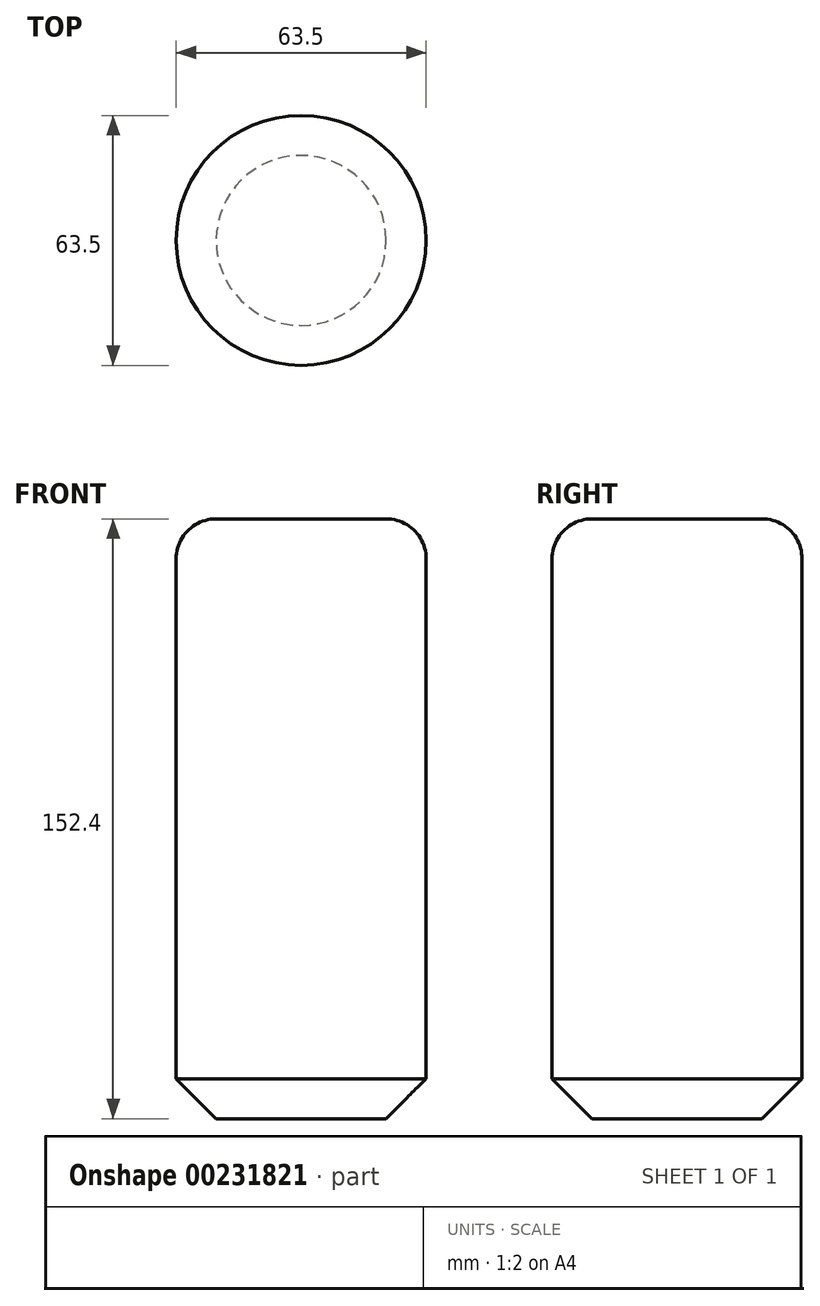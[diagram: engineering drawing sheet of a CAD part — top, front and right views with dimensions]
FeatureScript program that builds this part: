
annotation { "Feature Type Name" : "Feature", "Feature Type Description" : "" }
export const myFeature = defineFeature(function(context is Context, id is Id, definition is map)
    precondition{}
    {
        {
            var Q0;
            Q0=qCreatedBy(makeId("Top.planeOp"),FACE);
            var sketch = newSketch(context, id + "F0", { "sketchPlane" : qUnion([Q0])});
            skCircle(sketch, "E0", {"center": v(0, 0) * mm, "radius": 31.75 * mm});
            skSolve(sketch);
        }
        {
            var Q0;
            Q0=makeQuery(id+"F0.imprint","IMPRINT",FACE,{"disambiguationData":[TD([[makeQuery(id+"F0.imprint","IMPRINT",EDGE,{"derivedFrom":sQuery(id+"F0.wireOp",EDGE,"E0")}),1.0]])]});
            extrude(context, id + "F1", {"entities" : qUnion([Q0]), "oppositeDirection" : true, "depth" : 76.2 * mm, "hasSecondDirection" : true, "secondDirectionOppositeDirection" : false, "secondDirectionDepth" : 76.2 * mm});
        }
        {
            var Q0;
            Q0=makeQuery(id+"F1.opExtrude","CAP_EDGE",EDGE,{"disambiguationData":[OSD([sQuery(id+"F0.wireOp",EDGE,"E0")])],"isStart":true});
            fillet(context, id + "F2", {"entities" : qUnion([Q0]), "radius" : 10.16 * mm, "allowEdgeOverflow" : false});
        }
        {
            var Q0;
            Q0=makeQuery(id+"F1.opExtrude","CAP_EDGE",EDGE,{"disambiguationData":[OSD([sQuery(id+"F0.wireOp",EDGE,"E0")])],"isStart":false});
            chamfer(context, id + "F3", {"entities" : qUnion([Q0]), "width" : 10.16 * mm, "tangentPropagation" : true});
        }
    });
